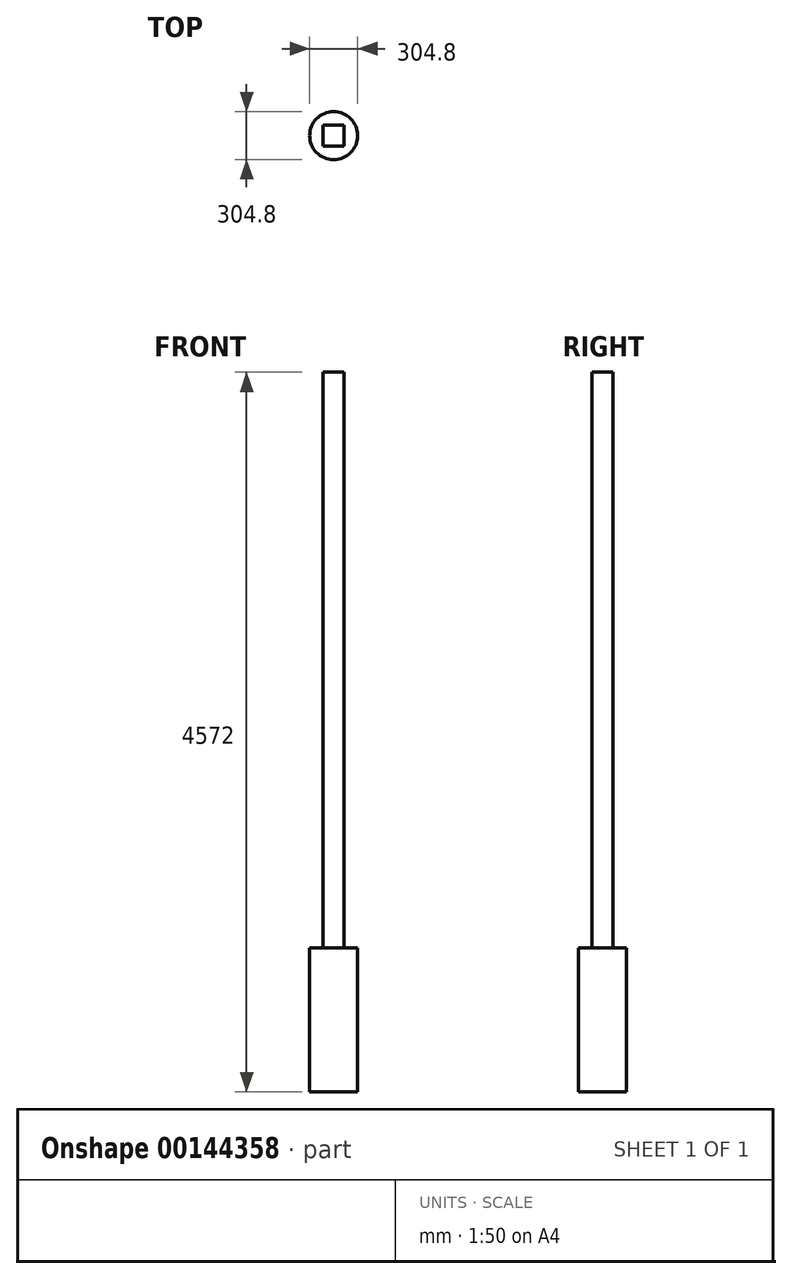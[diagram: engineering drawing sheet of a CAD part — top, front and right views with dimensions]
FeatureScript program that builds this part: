
annotation { "Feature Type Name" : "Feature", "Feature Type Description" : "" }
export const myFeature = defineFeature(function(context is Context, id is Id, definition is map)
    precondition{}
    {
        {
            var Q0;
            Q0=qCreatedBy(makeId("Top.planeOp"),FACE);
            var sketch = newSketch(context, id + "F0", { "sketchPlane" : qUnion([Q0])});
            skCircle(sketch, "E0", {"center": v(0, 0) * mm, "radius": 152.4 * mm});
            skSolve(sketch);
        }
        {
            var Q0;
            Q0 = qSketchRegion(id + "F0", true);
            extrude(context, id + "F1", {"entities" : qUnion([Q0]), "oppositeDirection" : true, "depth" : 914.4 * mm});
        }
        {
            var Q0;
            Q0=makeQuery(id+"F1.opExtrude","CAP_FACE",FACE,{"disambiguationData":[OSD([sQuery(id+"F0.wireOp",EDGE,"E0")])],"isStart":true});
            var sketch = newSketch(context, id + "F2", { "sketchPlane" : qUnion([Q0])});
            skLineSegment(sketch, "E1.bottom", {"start": v(-66.68, 66.68) * mm, "end": v(66.68, 66.68) * mm});
            skLineSegment(sketch, "E1.top", {"start": v(-66.68, -66.68) * mm, "end": v(66.68, -66.67) * mm});
            skLineSegment(sketch, "E1.left", {"start": v(-66.68, 66.67) * mm, "end": v(-66.68, -66.68) * mm});
            skLineSegment(sketch, "E1.right", {"start": v(66.68, 66.68) * mm, "end": v(66.68, -66.67) * mm});
            skSolve(sketch);
        }
        {
            var Q0;
            Q0 = qSketchRegion(id + "F2", true);
            extrude(context, id + "F3", {"entities" : qUnion([Q0]), "operationType" : NewBodyOperationType.ADD, "depth" : 3657.6 * mm});
        }
    });
